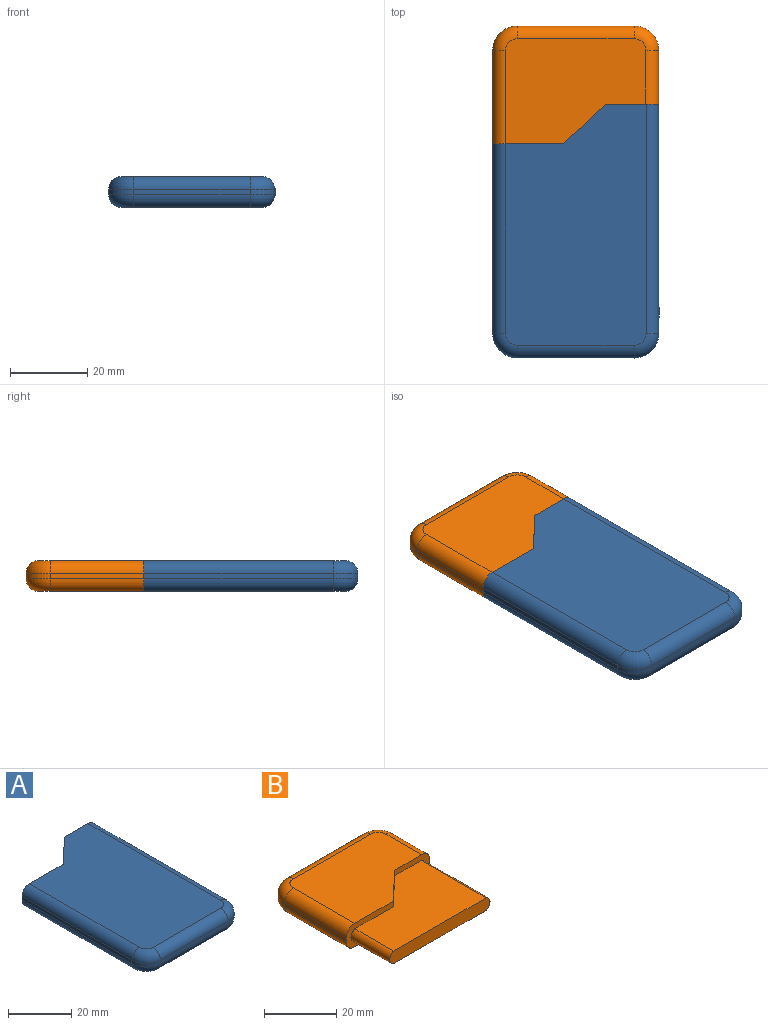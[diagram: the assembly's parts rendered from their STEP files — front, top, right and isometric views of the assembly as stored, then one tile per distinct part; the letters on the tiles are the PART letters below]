
ASSEMBLY  parts=2 mates=1
PART A: 90 faces, bbox 43.1x65.7x8 mm
  f0: plane 3.24x2.33mm, normal (1,0,0), area 5mm2, adj f37,f38,f39,f40,f41,f42,f43,f44
  f1: plane 1.4x0.75mm, normal (1,0,0), area 1.1mm2, adj f2,f3,f8,f32
  f2: cylinder r=3.3mm len=59.39mm, axis (0,1,0), area 304.6mm2, adj f1,f4,f9,f14,f18,f28,f32,f33
  f3: cylinder r=3.3mm len=59.39mm, axis (0,-1,0), area 304.3mm2, adj f1,f4,f9,f13,f22,f28,f29,f30
  f4: plane 13.8x8mm, normal (0,1,0), area 40.2mm2, adj f2,f3,f5,f9,f10,f13,f14,f23
  f5: plane 10.83x10.22mm, normal (-0.69,0.73,0), area 18.9mm2, adj f4,f11,f13,f23
  f6: cylinder r=6.35mm len=6.35mm, axis (0,0,-1), area 13.9mm2, adj f7,f12,f16,f20
  f7: plane 30.3x1.4mm, normal (0,-1,0), area 42.3mm2, adj f6,f8,f17,f21
  f8: cylinder r=6.35mm len=6.35mm, axis (0,0,-1), area 13.9mm2, adj f1,f7,f18,f22
  f9: plane 52.27x1.4mm, normal (1,0,0), area 73mm2, adj f2,f3,f4,f28
  f10: plane 10.83x10.22mm, normal (-0.69,0.73,0), area 18.9mm2, adj f4,f11,f14,f25
  f11: plane 18.37x8mm, normal (0,1,0), area 51.9mm2, adj f5,f10,f12,f13,f14,f15,f19,f23
  f12: plane 49.17x1.4mm, normal (-1,0,0), area 68.6mm2, adj f6,f11,f15,f19
  f13: plane 62.43x36.4mm, normal (0,0,1), area 2059.1mm2, adj f3,f4,f5,f11,f19,f20,f21,f22
  f14: plane 62.43x36.4mm, normal (0,0,-1), area 2059.1mm2, adj f2,f4,f10,f11,f15,f16,f17,f18
  f15: cylinder r=3.3mm len=49.17mm, axis (0,-1,0), area 255mm2, adj f11,f12,f14,f16
  f16: torus R=3.05mm, axis (0,0,1), area 42mm2, adj f6,f14,f15,f17
  f17: cylinder r=3.3mm len=30.3mm, axis (1,0,0), area 157.2mm2, adj f7,f14,f16,f18
  f18: torus R=3.05mm, axis (0,0,1), area 42mm2, adj f2,f8,f14,f17
  f19: cylinder r=3.3mm len=49.17mm, axis (0,1,0), area 255mm2, adj f11,f12,f13,f20
  f20: torus R=3.05mm, axis (0,0,1), area 42mm2, adj f6,f13,f19,f21
  f21: cylinder r=3.3mm len=30.3mm, axis (-1,0,0), area 157.2mm2, adj f7,f13,f20,f22
  f22: torus R=3.05mm, axis (0,0,1), area 42mm2, adj f3,f8,f13,f21
  f23: plane 36.4x25.4mm, normal (0,0,-1), area 715.2mm2, adj f4,f5,f11,f24,f26,f27
  f24: cylinder r=2.85mm len=25.4mm, axis (0,1,0), area 185.3mm2, adj f4,f23,f25,f27
  f25: plane 36.4x25.4mm, normal (0,0,1), area 715.2mm2, adj f4,f10,f11,f24,f26,f27
  f26: cylinder r=2.85mm len=15.18mm, axis (0,1,0), area 110.7mm2, adj f11,f23,f25,f27
  f27: plane 40.46x5.46mm, normal (0,1,0), area 215mm2, adj f23,f24,f25,f26
  f28: plane 1.98x0.51mm, normal (0,-1,0), area 1mm2, adj f2,f3,f9,f29,f35,f36
  f29: cylinder r=0.42mm len=0.49mm, axis (1,0,0), area 0.2mm2, adj f3,f28,f30,f36
  f30: plane 5.66x0.45mm, normal (0,0,-1), area 2.6mm2, adj f3,f29,f31,f36
  f31: cylinder r=0.42mm len=0.49mm, axis (1,0,0), area 0.2mm2, adj f3,f30,f32,f36
  f32: plane 1.98x0.51mm, normal (0,1,0), area 1mm2, adj f1,f2,f3,f31,f33,f36
  f33: cylinder r=0.48mm len=0.5mm, axis (1,0,0), area 0.2mm2, adj f2,f32,f34,f36
  f34: plane 5.66x0.46mm, normal (0,0,1), area 2.6mm2, adj f2,f33,f35,f36
  f35: cylinder r=0.48mm len=0.5mm, axis (1,0,0), area 0.2mm2, adj f2,f28,f34,f36
  f36: plane 6.36x2.53mm, normal (1,0,0), area 8.5mm2, adj f28,f29,f30,f31,f32,f33,f34,f35
  f37: cylinder r=0.36mm len=0.51mm, axis (-1,0,0), area 0.2mm2, adj f0,f36,f38,f44
  f38: plane 1.74x0.51mm, normal (0,-1,0), area 0.9mm2, adj f0,f36,f37,f39
  f39: cylinder r=0.36mm len=0.51mm, axis (-1,0,0), area 0.2mm2, adj f0,f36,f38,f40
  f40: plane 2.62x0.51mm, normal (0,0,-1), area 1.3mm2, adj f0,f36,f39,f41
  f41: cylinder r=0.36mm len=0.51mm, axis (-1,0,0), area 0.2mm2, adj f0,f36,f40,f42
  f42: plane 1.74x0.51mm, normal (0,1,0), area 0.9mm2, adj f0,f36,f41,f43
  f43: cylinder r=0.36mm len=0.51mm, axis (-1,0,0), area 0.2mm2, adj f0,f36,f42,f44
  f44: plane 2.62x0.51mm, normal (0,0,1), area 1.3mm2, adj f0,f36,f37,f43
  f45: plane 1.62x0.1mm, normal (0,1,0), area 0.2mm2, adj f0,f46,f48,f71
  f46: cylinder r=0.14mm len=0.27mm, axis (-1,0,0), area 0mm2, adj f0,f45,f47,f70
  f47: plane 1.62x0.1mm, normal (0,-1,0), area 0.2mm2, adj f0,f46,f48,f72
  f48: cylinder r=0.14mm len=0.27mm, axis (-1,0,0), area 0mm2, adj f0,f45,f47,f73
  f49: plane 1.84x0.22mm, normal (1,0,0), area 0.4mm2, adj f70,f71,f72,f73
  f50: plane 1.62x0.1mm, normal (0,1,0), area 0.2mm2, adj f0,f51,f53,f75
  f51: cylinder r=0.14mm len=0.27mm, axis (-1,0,0), area 0mm2, adj f0,f50,f52,f74
  f52: plane 1.62x0.1mm, normal (0,-1,0), area 0.2mm2, adj f0,f51,f53,f76
  f53: cylinder r=0.14mm len=0.27mm, axis (-1,0,0), area 0mm2, adj f0,f50,f52,f77
  f54: plane 1.84x0.22mm, normal (1,0,0), area 0.4mm2, adj f74,f75,f76,f77
  f55: plane 1.62x0.1mm, normal (0,1,0), area 0.2mm2, adj f0,f56,f58,f83
  f56: cylinder r=0.14mm len=0.27mm, axis (-1,0,0), area 0mm2, adj f0,f55,f57,f82
  f57: plane 1.62x0.1mm, normal (0,-1,0), area 0.2mm2, adj f0,f56,f58,f84
  f58: cylinder r=0.14mm len=0.27mm, axis (-1,0,0), area 0mm2, adj f0,f55,f57,f85
  f59: plane 1.84x0.22mm, normal (1,0,0), area 0.4mm2, adj f82,f83,f84,f85
  f60: plane 1.62x0.1mm, normal (0,1,0), area 0.2mm2, adj f0,f61,f63,f87
  f61: cylinder r=0.14mm len=0.27mm, axis (-1,0,0), area 0mm2, adj f0,f60,f62,f89
  f62: plane 1.62x0.1mm, normal (0,-1,0), area 0.2mm2, adj f0,f61,f63,f88
  f63: cylinder r=0.14mm len=0.27mm, axis (-1,0,0), area 0mm2, adj f0,f60,f62,f86
  f64: plane 1.84x0.22mm, normal (1,0,0), area 0.4mm2, adj f86,f87,f88,f89
  f65: plane 1.62x0.1mm, normal (0,1,0), area 0.2mm2, adj f0,f66,f68,f79
  f66: cylinder r=0.14mm len=0.27mm, axis (-1,0,0), area 0mm2, adj f0,f65,f67,f78
  f67: plane 1.62x0.1mm, normal (0,-1,0), area 0.2mm2, adj f0,f66,f68,f80
  f68: cylinder r=0.14mm len=0.27mm, axis (-1,0,0), area 0mm2, adj f0,f65,f67,f81
  f69: plane 1.84x0.22mm, normal (1,0,0), area 0.4mm2, adj f78,f79,f80,f81
  f70: cone r=0.11mm half-angle=45deg, axis (-1,0,0), area 0mm2, adj f46,f49,f71,f72
  f71: plane 1.62x0.03mm, normal (0.71,0.71,0), area 0.1mm2, adj f45,f49,f70,f73
  f72: plane 1.62x0.03mm, normal (0.71,-0.71,0), area 0.1mm2, adj f47,f49,f70,f73
  f73: cone r=0.14mm half-angle=45deg, axis (-1,0,0), area 0mm2, adj f48,f49,f71,f72
  f74: cone r=0.11mm half-angle=45deg, axis (-1,0,0), area 0mm2, adj f51,f54,f75,f76
  f75: plane 1.62x0.03mm, normal (0.71,0.71,0), area 0.1mm2, adj f50,f54,f74,f77
  f76: plane 1.62x0.03mm, normal (0.71,-0.71,0), area 0.1mm2, adj f52,f54,f74,f77
  f77: cone r=0.14mm half-angle=45deg, axis (-1,0,0), area 0mm2, adj f53,f54,f75,f76
  f78: cone r=0.11mm half-angle=45deg, axis (-1,0,0), area 0mm2, adj f66,f69,f79,f80
  f79: plane 1.62x0.03mm, normal (0.71,0.71,0), area 0.1mm2, adj f65,f69,f78,f81
  f80: plane 1.62x0.03mm, normal (0.71,-0.71,0), area 0.1mm2, adj f67,f69,f78,f81
  f81: cone r=0.14mm half-angle=45deg, axis (-1,0,0), area 0mm2, adj f68,f69,f79,f80
  f82: cone r=0.11mm half-angle=45deg, axis (-1,0,0), area 0mm2, adj f56,f59,f83,f84
  f83: plane 1.62x0.03mm, normal (0.71,0.71,0), area 0.1mm2, adj f55,f59,f82,f85
  f84: plane 1.62x0.03mm, normal (0.71,-0.71,0), area 0.1mm2, adj f57,f59,f82,f85
  f85: cone r=0.14mm half-angle=45deg, axis (-1,0,0), area 0mm2, adj f58,f59,f83,f84
  f86: cone r=0.14mm half-angle=45deg, axis (-1,0,0), area 0mm2, adj f63,f64,f87,f88
  f87: plane 1.62x0.03mm, normal (0.71,0.71,0), area 0.1mm2, adj f60,f64,f86,f89
  f88: plane 1.62x0.03mm, normal (0.71,-0.71,0), area 0.1mm2, adj f62,f64,f86,f89
  f89: cone r=0.11mm half-angle=45deg, axis (-1,0,0), area 0mm2, adj f61,f64,f87,f88
PART B: 26 faces, bbox 43x45.7x8 mm
  f0: plane 18.37x8mm, normal (0,-1,0), area 73.8mm2, adj f1,f4,f5,f9,f10,f11,f16,f21
  f1: plane 10.83x10.22mm, normal (0.69,-0.73,0), area 27.8mm2, adj f0,f6,f10,f22
  f2: plane 30.3x1.4mm, normal (0,1,0), area 42.3mm2, adj f3,f8,f13,f18
  f3: cylinder r=6.35mm len=6.35mm, axis (0,0,-1), area 13.9mm2, adj f2,f4,f12,f17
  f4: plane 24.13x1.4mm, normal (-1,0,0), area 33.7mm2, adj f0,f3,f11,f16
  f5: plane 10.83x10.22mm, normal (0.69,-0.73,0), area 27.9mm2, adj f0,f6,f9,f23
  f6: plane 13.8x8mm, normal (0,-1,0), area 56.6mm2, adj f1,f5,f7,f9,f10,f15,f20,f22
  f7: plane 13.91x1.4mm, normal (1,0,0), area 19.4mm2, adj f6,f8,f15,f20
  f8: cylinder r=6.35mm len=6.35mm, axis (0,0,-1), area 13.9mm2, adj f2,f7,f14,f19
  f9: plane 36.4x27.18mm, normal (0,0,1), area 822.6mm2, adj f0,f5,f6,f16,f17,f18,f19,f20
  f10: plane 36.4x27.18mm, normal (0,0,-1), area 822.6mm2, adj f0,f1,f6,f11,f12,f13,f14,f15
  f11: cylinder r=3.3mm len=24.13mm, axis (0,-1,0), area 125.2mm2, adj f0,f4,f10,f12
  f12: torus R=3.05mm, axis (0,0,1), area 42mm2, adj f3,f10,f11,f13
  f13: cylinder r=3.3mm len=30.3mm, axis (-1,0,0), area 157.2mm2, adj f2,f10,f12,f14
  f14: torus R=3.05mm, axis (0,0,1), area 42mm2, adj f8,f10,f13,f15
  f15: cylinder r=3.3mm len=13.91mm, axis (0,1,0), area 72.2mm2, adj f6,f7,f10,f14
  f16: cylinder r=3.3mm len=24.13mm, axis (0,1,0), area 125.2mm2, adj f0,f4,f9,f17
  f17: torus R=3.05mm, axis (0,0,1), area 42mm2, adj f3,f9,f16,f18
  f18: cylinder r=3.3mm len=30.3mm, axis (1,0,0), area 157.2mm2, adj f2,f9,f17,f19
  f19: torus R=3.05mm, axis (0,0,1), area 42mm2, adj f8,f9,f18,f20
  f20: cylinder r=3.3mm len=13.91mm, axis (0,-1,0), area 72.2mm2, adj f6,f7,f9,f19
  f21: cylinder r=2.24mm len=15.18mm, axis (0,1,0), area 85.1mm2, adj f0,f22,f23,f25
  f22: plane 36.22x25.4mm, normal (0,0,-1), area 711.7mm2, adj f0,f1,f6,f21,f24,f25
  f23: plane 36.22x25.4mm, normal (0,0,1), area 711.7mm2, adj f0,f5,f6,f21,f24,f25
  f24: cylinder r=2.24mm len=25.4mm, axis (0,1,0), area 142.3mm2, adj f6,f22,f23,f25
  f25: plane 39.29x4.26mm, normal (0,-1,0), area 163.7mm2, adj f21,f22,f23,f24
PLACE A t=(-12.53,-342.1,-55.64)mm
PLACE B t=(52.97,-286.25,-55.64)mm
MATE slider A.f27 <-> B.f25  axis (0,1,0) through (8.97,-301.77,-51.64)mm
